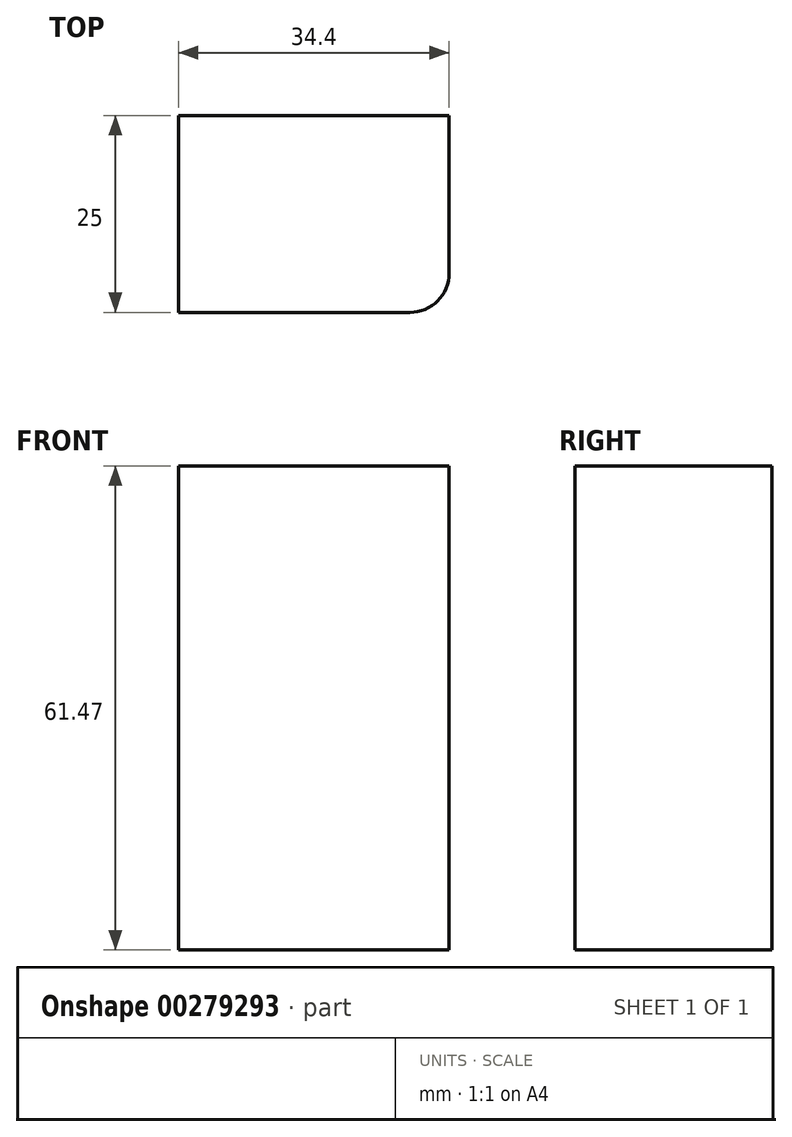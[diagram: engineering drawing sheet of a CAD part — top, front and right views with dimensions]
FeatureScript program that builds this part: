
annotation { "Feature Type Name" : "Feature", "Feature Type Description" : "" }
export const myFeature = defineFeature(function(context is Context, id is Id, definition is map)
    precondition{}
    {
        {
            var Q0;
            Q0=qCreatedBy(makeId("Front.planeOp"),FACE);
            var sketch = newSketch(context, id + "F0", { "sketchPlane" : qUnion([Q0])});
            skLineSegment(sketch, "E0.bottom", {"start": v(-91.85, 47.48) * mm, "end": v(-57.45, 47.48) * mm});
            skLineSegment(sketch, "E0.top", {"start": v(-91.85, -13.99) * mm, "end": v(-57.45, -13.99) * mm});
            skLineSegment(sketch, "E0.left", {"start": v(-91.85, 47.48) * mm, "end": v(-91.85, -13.99) * mm});
            skLineSegment(sketch, "E0.right", {"start": v(-57.45, 47.48) * mm, "end": v(-57.45, -13.99) * mm});
            skSolve(sketch);
        }
        {
            var Q0;
            Q0=makeQuery(id+"F0.imprint","IMPRINT",FACE,{"disambiguationData":[TD([[makeQuery(id+"F0.imprint","IMPRINT",EDGE,{"derivedFrom":sQuery(id+"F0.wireOp",EDGE,"E0.bottom")}),-1.0]])]});
            extrude(context, id + "F1", {"entities" : qUnion([Q0]), "depth" : 25 * mm});
        }
        {
            var Q0;
            Q0=makeQuery(id+"F1.opExtrude","CAP_EDGE",EDGE,{"disambiguationData":[OSD([sQuery(id+"F0.wireOp",EDGE,"E0.right")])],"isStart":false});
            fillet(context, id + "F2", {"entities" : qUnion([Q0]), "radius" : 5 * mm, "tangentPropagation" : true, "allowEdgeOverflow" : false});
        }
    });
